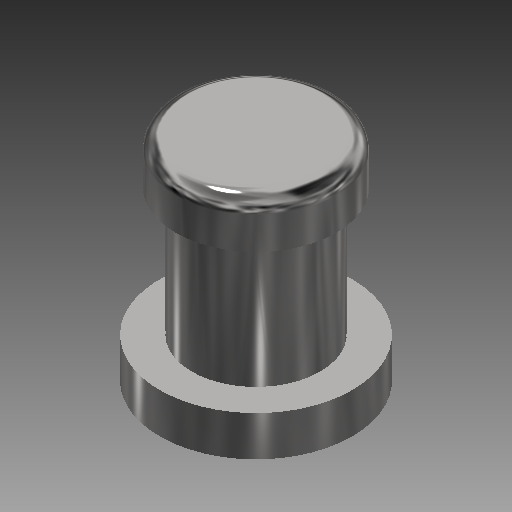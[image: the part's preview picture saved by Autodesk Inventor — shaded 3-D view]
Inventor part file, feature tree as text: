
AUTODESK INVENTOR PART (.ipt)
format: ipt  version: 2019 (Build 230136000, 136)  size: 157,184 bytes
history: native  units: mm
features: revolve x1, sketch x1
ambient origin geometry x8: Origin, YZ Plane, XZ Plane, XY Plane, X Axis, Y Axis, Z Axis, Center Point
bodies: Solid1 (feature_tree)
feature tree (2):
  revolve  "Revolution1"  [1 undecoded]
  sketch  "Sketch1"  dims[d1=10.0mm d2=8.0mm d3=12.0mm d4=8.0mm d5=3.0mm d6=2.5mm d7=1.0mm d8=90.0deg]
note: 1 required parameter value undecoded (feature->parameter linkage not recoverable at this tier; creation-order binding heuristic only, values carry confidence <= 0.55)
